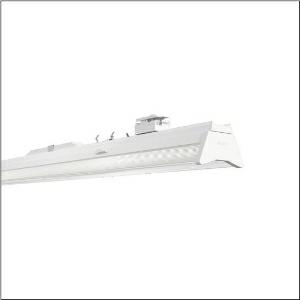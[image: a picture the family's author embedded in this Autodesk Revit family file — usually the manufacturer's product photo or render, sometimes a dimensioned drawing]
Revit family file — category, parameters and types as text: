
# Revit family: licross_21_performance_mo_52tm167n46xg
name_source: partatom
category: Lighting Fixtures
units: mm (PartAtom-declared; Revit-internal decimal feet)

## family parameters
Cut with Voids When Loaded = No
Host = Face
Light Source = No
Part Type = Normal
Room Calculation Point = No
Round Connector Dimension = Use Diameter
Shared = No

## types (1)
- Licross 21 Performance MO (1 x LED, 6000 lm, 32.4 W, 4000K)
    Apparent Load = 32 VA
    CIE Flux Codes = 66 88 96 79 100
    Color Rendering = 80
    Color Temperature = 4000K
    Default Elevation = 1800 mm
    Description = Licross 21 Performance MO, luminaire insert, of sheet steel, galvanised, coil coated, white, length: 1.500mm, width: 120mm, height: 123mm, LED rated luminous flux: 6.000lm, light colour: 840, SDCM (Standard Deviation of Colour Matching)MacAdam ≤ 3 SDCM (initial), control gear: ON/OFF, with plug, 3-pole, with phase selection, mains connection: 220..240V, AC, 50/60Hz, rated input power: 32W, internal wiring halogen-free, primary light control with lens, of plastic, primary optical cover: cover, of PMMA, light emission: direct/indirect distribution, primary light characteristic: symmetric, protection rating (complete): IP40, insulation class (complete): insulation class I (protective earthing), certification: CE, ENEC, UKCA, protection symbol: D if used in an environment without relevant dust loads with corresponding accessories, impact resistance: IK06, permissible ambient temperature for indoor applications: -35..+50°C, corresponds to IFS (International Featured Standards) requirements for safety and quality in the food industry, reducing of maximum allowable ambient temperature of 5°C with ceiling mounting, LABS conformity tested according to VDMA 24364:2018-05, The light source and the operating device comply with the requirements of the Ecodesign Regulation (EU) 2019/2020 and are replaceable in accordance with this regulation, packaging unit: 1 piece
    Height = 114 mm
    Lamp = 1 x LED
    Lamp Light Flux = 6000 lm
    Lamp Power = 32.4 W
    Lamp count = 1
    Length = 1500 mm
    Luminous efficacy = 185 lm/W
    Manufacturer = Siteco
    ModVariant = No
    Model = 52TM167N46XG
    Mounting Place = Ceiling
    Mounting Type = Pendant
    Number of Poles = 1
    OnlyDefault = Yes
    Power Factor = 1
    Product Name = Licross 21 Performance MO
    Product group = luminaire insert | ceiling pendant
    ProductGroupID = 901
    Protection Class = Protection class I
    Protection Degree = IP 40
    RLX_Detail_Level = 1
    RLX_Emergency_Light_Flux = 0 lm
    RLX_Emergency_Type = 0
    RLX_Emergency_Type_DB = No
    RlxData = <blob elided: 30625 chars, md5=fa028430>
    Socket = socket
    Standby Power = 0 W
    System Light Flux = 6000 lm
    System Power = 32 W
    Type Comments = Product without accessories
    Type Image = l_1256138.jpg
    URL = http://relux.com
    VarID = ---
    Voltage = 0 V
    Weight = 0.00 kg
    Width = 120 mm

## geometry (parser evidence)
native form markers: Blend x4, Sweep x13
no freeform markers — native parametric forms only
